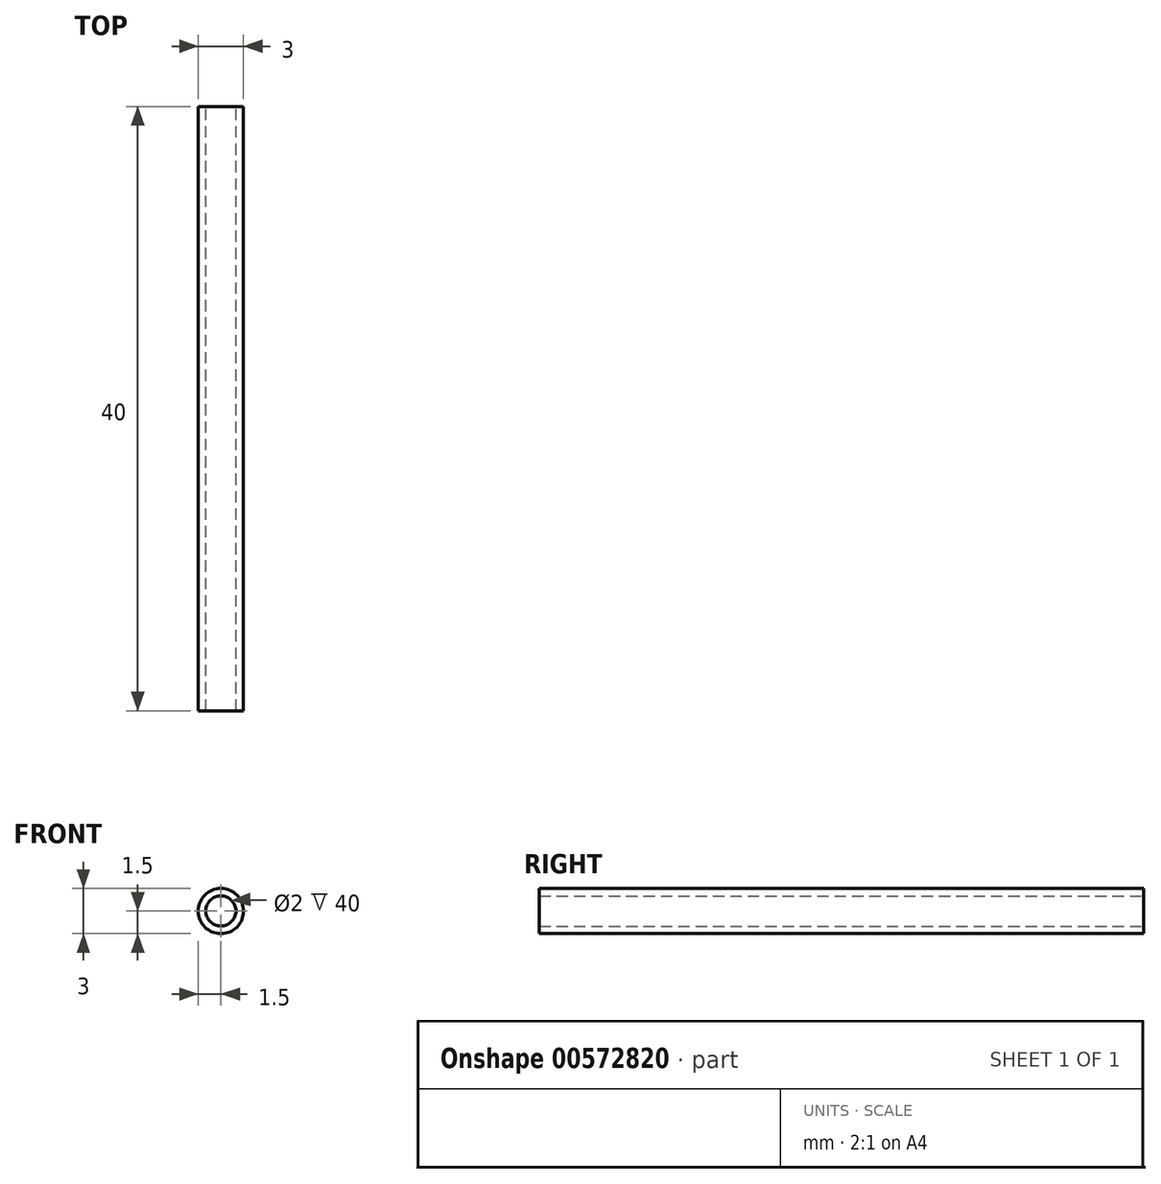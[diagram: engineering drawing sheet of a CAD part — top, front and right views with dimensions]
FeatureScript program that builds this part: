
annotation { "Feature Type Name" : "Feature", "Feature Type Description" : "" }
export const myFeature = defineFeature(function(context is Context, id is Id, definition is map)
    precondition{}
    {
        {
            var Q0;
            Q0=qCreatedBy(makeId("Front.planeOp"),FACE);
            var sketch = newSketch(context, id + "F0", { "sketchPlane" : qUnion([Q0])});
            skCircle(sketch, "E0", {"center": v(0, 0) * mm, "radius": 1.5 * mm});
            skCircle(sketch, "E1", {"center": v(0, 0) * mm, "radius": 1 * mm});
            skSolve(sketch);
        }
        {
            var Q0;
            Q0 = qSketchRegion(id + "F0", true);
            extrude(context, id + "F1", {"entities" : qUnion([Q0]), "depth" : 40 * mm, "offsetDistance" : 25 * mm});
        }
    });
